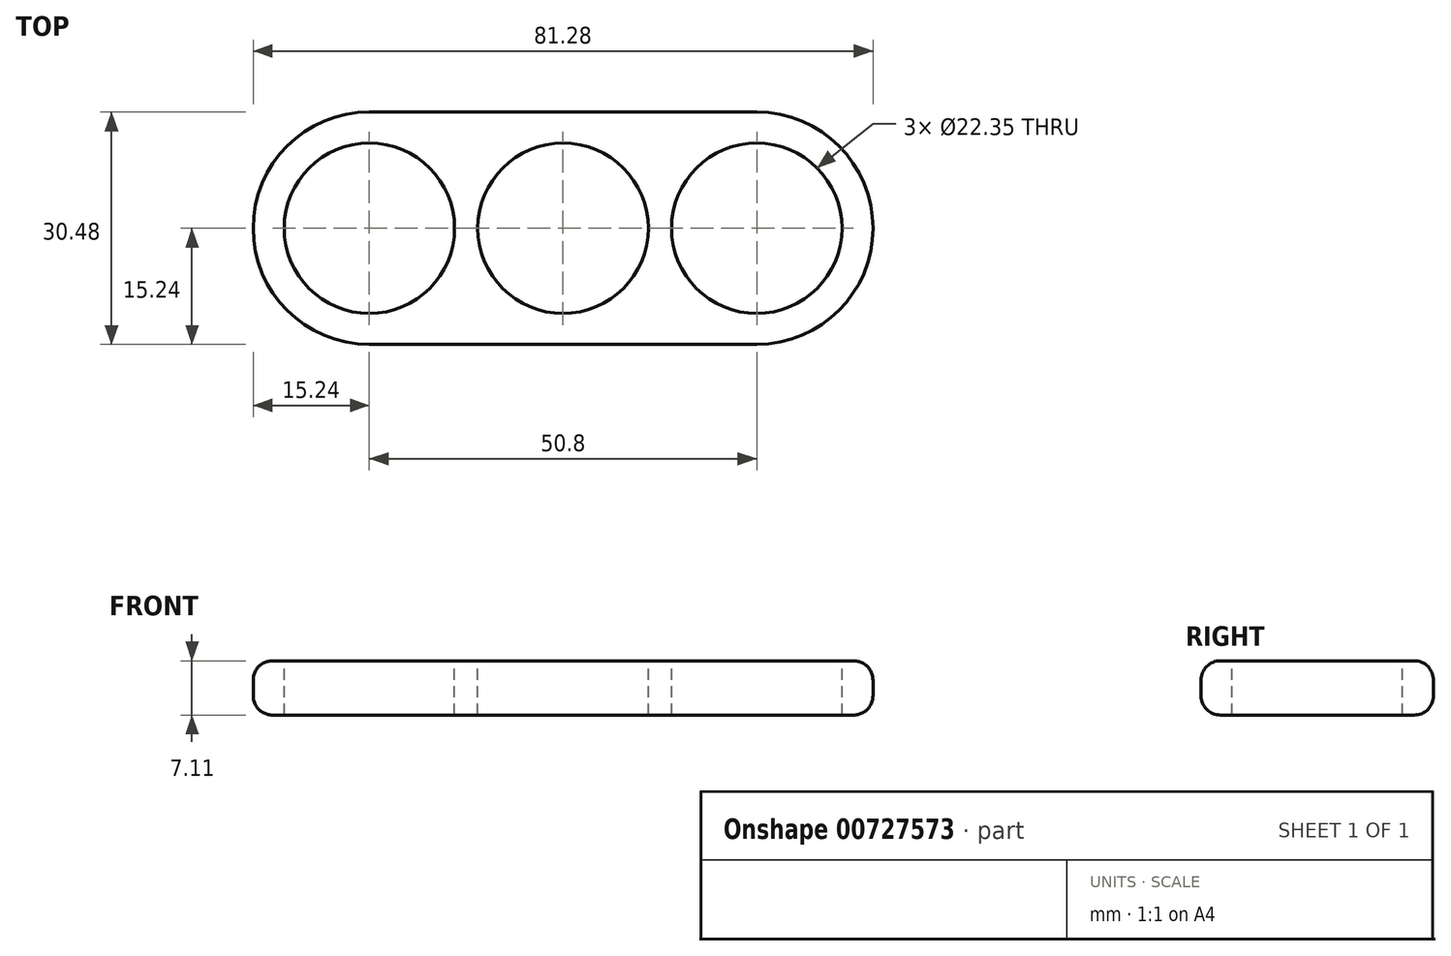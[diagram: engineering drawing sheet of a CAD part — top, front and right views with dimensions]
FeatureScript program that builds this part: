
annotation { "Feature Type Name" : "Feature", "Feature Type Description" : "" }
export const myFeature = defineFeature(function(context is Context, id is Id, definition is map)
    precondition{}
    {
        {
            var Q0;
            Q0=qCreatedBy(makeId("Top.planeOp"),FACE);
            var sketch = newSketch(context, id + "F0", { "sketchPlane" : qUnion([Q0])});
            skLineSegment(sketch, "E0.bottom", {"start": v(25.4, 15.24) * mm, "end": v(-25.4, 15.24) * mm});
            skLineSegment(sketch, "E0.top", {"start": v(25.4, -15.24) * mm, "end": v(-25.4, -15.24) * mm});
            skLineSegment(sketch, "E0.left", {"start": v(25.4, 15.24) * mm, "end": v(25.4, -15.24) * mm});
            skLineSegment(sketch, "E0.right", {"start": v(-25.4, 15.24) * mm, "end": v(-25.4, -15.24) * mm});
            skPoint(sketch, "E0.middle", {"position": v(0, 0) * mm});
            skArc(sketch, "E1", {"start": v(-25.4, 15.24) * mm, "mid": v(-40.64, 0) * mm, "end": v(-25.4, -15.24) * mm});
            skArc(sketch, "E2", {"start": v(25.4, -15.24) * mm, "mid": v(40.64, 0) * mm, "end": v(25.4, 15.24) * mm});
            skSolve(sketch);
        }
        {
            var Q0;
            Q0 = qSketchRegion(id + "F0", true);
            extrude(context, id + "F1", {"entities" : qUnion([Q0]), "depth" : 7.11 * mm, "offsetDistance" : 25.4 * mm});
        }
        {
            var Q0;
            Q0=makeQuery(id+"F1.opExtrude","CAP_FACE",FACE,{"disambiguationData":[OSD([sQuery(id+"F0.wireOp",EDGE,"E0.bottom"),sQuery(id+"F0.wireOp",EDGE,"E0.top"),sQuery(id+"F0.wireOp",EDGE,"E1"),sQuery(id+"F0.wireOp",EDGE,"E2")])],"isStart":false});
            var sketch = newSketch(context, id + "F2", { "sketchPlane" : qUnion([Q0])});
            skCircle(sketch, "E3", {"center": v(0, 0) * mm, "radius": 11.18 * mm});
            skCircle(sketch, "E4", {"center": v(-25.4, 0) * mm, "radius": 11.18 * mm});
            skCircle(sketch, "E5", {"center": v(25.4, 0) * mm, "radius": 11.18 * mm});
            skSolve(sketch);
        }
        {
            var Q0;
            Q0 = qSketchRegion(id + "F2", true);
            extrude(context, id + "F3", {"entities" : qUnion([Q0]), "operationType" : NewBodyOperationType.REMOVE, "oppositeDirection" : true, "depth" : 25.4 * mm, "offsetDistance" : 25.4 * mm});
        }
        {
            var Q0;
            Q0=makeQuery(id+"F1.opExtrude","CAP_EDGE",EDGE,{"disambiguationData":[OSD([sQuery(id+"F0.wireOp",EDGE,"E0.bottom")])],"isStart":true});
            var Q1;
            Q1=makeQuery(id+"F1.opExtrude","CAP_EDGE",EDGE,{"disambiguationData":[OSD([sQuery(id+"F0.wireOp",EDGE,"E1")])],"isStart":true});
            var Q2;
            Q2=makeQuery(id+"F1.opExtrude","CAP_EDGE",EDGE,{"disambiguationData":[OSD([sQuery(id+"F0.wireOp",EDGE,"E0.top")])],"isStart":true});
            var Q3;
            Q3=makeQuery(id+"F1.opExtrude","CAP_EDGE",EDGE,{"disambiguationData":[OSD([sQuery(id+"F0.wireOp",EDGE,"E2")])],"isStart":true});
            var Q4;
            Q4=makeQuery(id+"F1.opExtrude","CAP_EDGE",EDGE,{"disambiguationData":[OSD([sQuery(id+"F0.wireOp",EDGE,"E2")])],"isStart":false});
            var Q5;
            Q5=makeQuery(id+"F1.opExtrude","CAP_EDGE",EDGE,{"disambiguationData":[OSD([sQuery(id+"F0.wireOp",EDGE,"E0.bottom")])],"isStart":false});
            var Q6;
            Q6=makeQuery(id+"F1.opExtrude","CAP_EDGE",EDGE,{"disambiguationData":[OSD([sQuery(id+"F0.wireOp",EDGE,"E1")])],"isStart":false});
            var Q7;
            Q7=makeQuery(id+"F1.opExtrude","CAP_EDGE",EDGE,{"disambiguationData":[OSD([sQuery(id+"F0.wireOp",EDGE,"E0.top")])],"isStart":false});
            fillet(context, id + "F4", {"entities" : qUnion([Q0, Q1, Q2, Q3, Q4, Q5, Q6, Q7]), "radius" : 2.54 * mm, "tangentPropagation" : true, "allowEdgeOverflow" : false});
        }
    });
